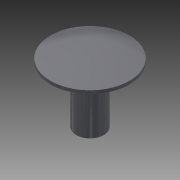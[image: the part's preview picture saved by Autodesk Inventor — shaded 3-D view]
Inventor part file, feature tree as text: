
AUTODESK INVENTOR PART (.ipt)
format: ipt  version: 2018 (Build 220112000, 112)  size: 91,648 bytes
history: native  units: mm (DEFAULTED — no unit token found)
features: sketch x2, reference x2, revolve x1, extrude x1
ambient origin geometry x8: Origin, YZ Plane, XZ Plane, XY Plane, X Axis, Y Axis, Z Axis, Center Point
bodies: Solid1 (feature_tree)
feature tree (6):
  revolve  "Revolution1"  [1 undecoded]
  extrude  "Extrusion1"  [1 undecoded]
  sketch  "Sketch1"  dims[d0=90.0deg d1=3.175mm d2=0.0mm]
  reference  "Reference1"
  reference  "Reference2"
  sketch  "Sketch2"
note: 2 required parameter values undecoded (feature->parameter linkage not recoverable at this tier; creation-order binding heuristic only, values carry confidence <= 0.55)